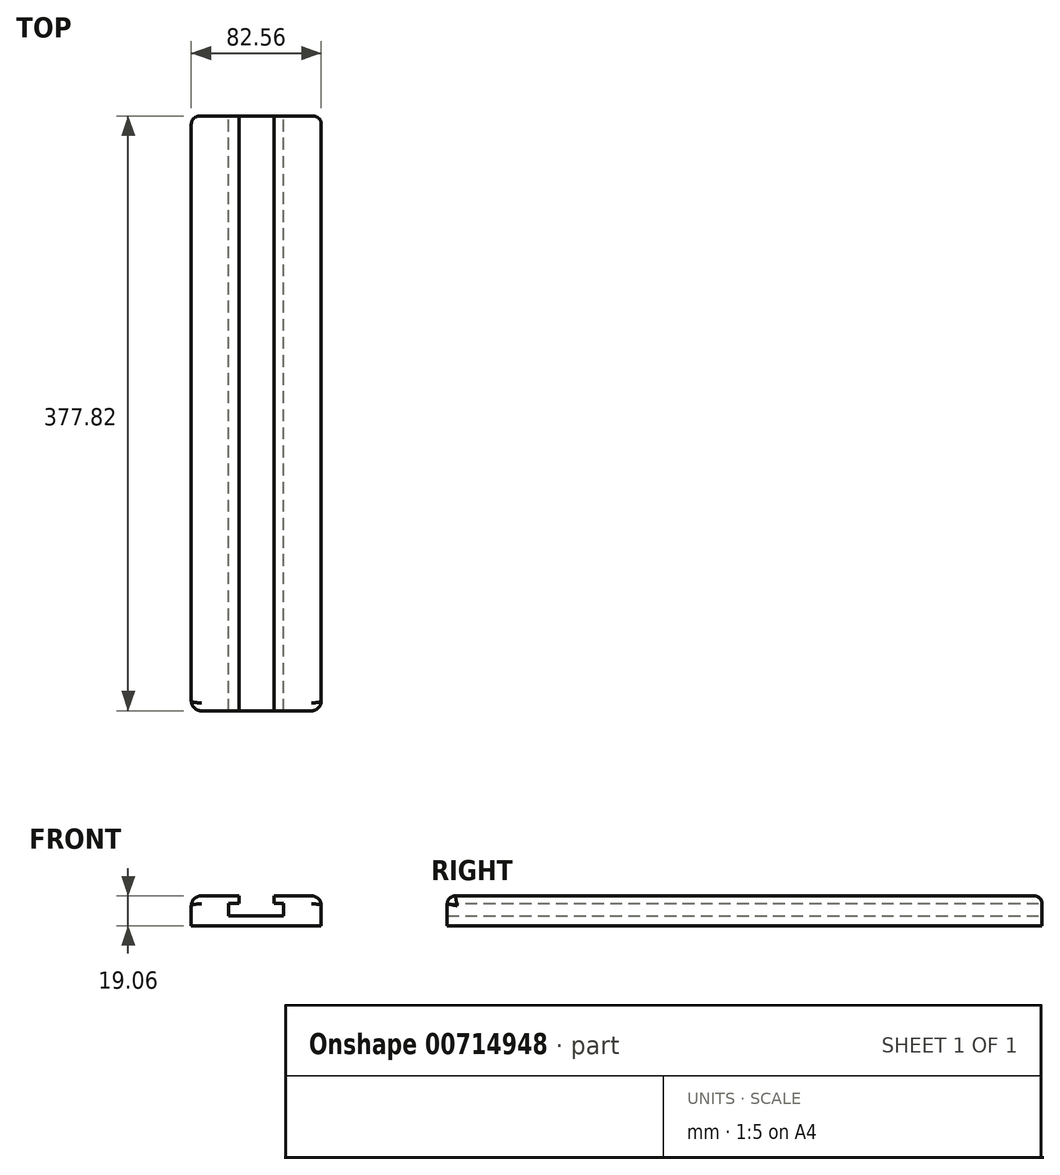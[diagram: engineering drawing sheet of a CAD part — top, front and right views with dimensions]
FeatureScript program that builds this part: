
annotation { "Feature Type Name" : "Feature", "Feature Type Description" : "" }
export const myFeature = defineFeature(function(context is Context, id is Id, definition is map)
    precondition{}
    {
        {
            var Q0;
            Q0=qCreatedBy(makeId("Front.planeOp"),FACE);
            var sketch = newSketch(context, id + "F0", { "sketchPlane" : qUnion([Q0])});
            skLineSegment(sketch, "E0.bottom", {"start": v(41.28, -9.52) * mm, "end": v(-41.28, -9.53) * mm});
            skLineSegment(sketch, "E0.left", {"start": v(41.28, -9.52) * mm, "end": v(41.28, 3.18) * mm});
            skLineSegment(sketch, "E0.right", {"start": v(-41.28, -9.53) * mm, "end": v(-41.28, 3.17) * mm});
            skPoint(sketch, "E0.middle", {"position": v(0, 0) * mm});
            skPoint(sketch, "E1.visualSharp", {"position": v(-41.28, 9.53) * mm});
            skPoint(sketch, "E2.visualSharp", {"position": v(41.28, 9.53) * mm});
            skArc(sketch, "E2.filletArc", {"start": v(41.28, 3.18) * mm, "mid": v(39.42, 7.67) * mm, "end": v(34.93, 9.53) * mm});
            skLineSegment(sketch, "E3.trimOffspring", {"start": v(-11.11, 9.53) * mm, "end": v(-34.93, 9.52) * mm});
            skLineSegment(sketch, "E4", {"start": v(34.93, 9.53) * mm, "end": v(11.11, 9.53) * mm});
            skPoint(sketch, "E5.end.orphan", {"position": v(11.11, 4.76) * mm});
            skPoint(sketch, "E6.right.end.orphan", {"position": v(10.19, 0) * mm});
            skLineSegment(sketch, "E7.bottom", {"start": v(-17.46, -3.18) * mm, "end": v(17.46, -3.17) * mm});
            skLineSegment(sketch, "E7.top", {"start": v(-17.46, 4.76) * mm, "end": v(-11.11, 4.76) * mm});
            skLineSegment(sketch, "E7.left", {"start": v(-17.46, -3.18) * mm, "end": v(-17.46, 4.76) * mm});
            skLineSegment(sketch, "E7.right", {"start": v(17.46, -3.17) * mm, "end": v(17.46, 4.76) * mm});
            skLineSegment(sketch, "E8", {"start": v(-11.11, 9.53) * mm, "end": v(-11.11, 4.76) * mm});
            skLineSegment(sketch, "E9", {"start": v(11.11, 9.53) * mm, "end": v(11.11, 4.76) * mm});
            skLineSegment(sketch, "E10.trimOffspring", {"start": v(11.11, 4.76) * mm, "end": v(17.46, 4.76) * mm});
            skPoint(sketch, "E1.filletArc.center.orphan", {"position": v(-34.93, 4.76) * mm});
            skPoint(sketch, "E11.visualSharp", {"position": v(-41.28, 9.52) * mm});
            skArc(sketch, "E11.filletArc", {"start": v(-34.93, 9.52) * mm, "mid": v(-39.42, 7.67) * mm, "end": v(-41.28, 3.17) * mm});
            skSolve(sketch);
        }
        {
            var Q0;
            Q0 = qSketchRegion(id + "F0", true);
            extrude(context, id + "F1", {"entities" : qUnion([Q0]), "endBound" : BoundingType.SYMMETRIC, "depth" : 377.82 * mm, "offsetDistance" : 25.4 * mm});
        }
        {
            var Q0;
            Q0=makeQuery(id+"F1.opExtrude","SWEPT_FACE",FACE,{"disambiguationData":[OSD([sQuery(id+"F0.wireOp",EDGE,"E0.bottom")])]});
            var sketch = newSketch(context, id + "F2", { "sketchPlane" : qUnion([Q0])});
            skLineSegment(sketch, "E12.bottom", {"start": v(-34.93, 188.91) * mm, "end": v(-34.93, 188.91) * mm});
            skLineSegment(sketch, "E12.left", {"start": v(-41.28, 182.56) * mm, "end": v(-41.28, 182.56) * mm});
            skPoint(sketch, "E13.visualSharp", {"position": v(-41.28, 188.91) * mm});
            skArc(sketch, "E13.filletArc", {"start": v(-34.93, 188.91) * mm, "mid": v(-39.42, 187.05) * mm, "end": v(-41.27, 182.56) * mm});
            skLineSegment(sketch, "E14", {"start": v(-34.93, 188.91) * mm, "end": v(-41.28, 188.91) * mm});
            skLineSegment(sketch, "E15", {"start": v(-41.28, 188.91) * mm, "end": v(-41.28, 182.56) * mm});
            skSolve(sketch);
        }
        {
            var Q0;
            Q0 = qSketchRegion(id + "F2", true);
            extrude(context, id + "F3", {"entities" : qUnion([Q0]), "operationType" : NewBodyOperationType.REMOVE, "oppositeDirection" : true, "depth" : 19.05 * mm, "offsetDistance" : 25.4 * mm});
        }
        {
            var Q0;
            Q0=makeQuery(id+"F1.opExtrude","SWEPT_FACE",FACE,{"disambiguationData":[OSD([sQuery(id+"F0.wireOp",EDGE,"E0.bottom")])]});
            var sketch = newSketch(context, id + "F4", { "sketchPlane" : qUnion([Q0])});
            skLineSegment(sketch, "E16.bottom", {"start": v(34.93, 188.91) * mm, "end": v(34.93, 188.91) * mm});
            skLineSegment(sketch, "E16.left", {"start": v(41.28, 182.56) * mm, "end": v(41.28, 182.56) * mm});
            skPoint(sketch, "E17.visualSharp", {"position": v(41.28, 188.91) * mm});
            skArc(sketch, "E17.filletArc", {"start": v(41.28, 182.56) * mm, "mid": v(39.42, 187.05) * mm, "end": v(34.93, 188.91) * mm});
            skLineSegment(sketch, "E18", {"start": v(34.93, 188.91) * mm, "end": v(41.28, 188.91) * mm});
            skLineSegment(sketch, "E19", {"start": v(41.28, 182.56) * mm, "end": v(41.28, 188.91) * mm});
            skSolve(sketch);
        }
        {
            var Q0;
            Q0 = qSketchRegion(id + "F4", true);
            extrude(context, id + "F5", {"entities" : qUnion([Q0]), "operationType" : NewBodyOperationType.REMOVE, "oppositeDirection" : true, "depth" : 19.05 * mm, "offsetDistance" : 25.4 * mm});
        }
        {
            var Q0;
            Q0=makeQuery(id+"F1.opExtrude","CAP_EDGE",EDGE,{"disambiguationData":[OSD([sQuery(id+"F0.wireOp",EDGE,"E3.trimOffspring")])],"isStart":false});
            var Q1;
            Q1=makeQuery(id+"F1.opExtrude","CAP_EDGE",EDGE,{"disambiguationData":[OSD([sQuery(id+"F0.wireOp",EDGE,"E4")])],"isStart":false});
            var Q2;
            Q2=makeQuery(id+"F1.opExtrude","CAP_EDGE",EDGE,{"disambiguationData":[OSD([sQuery(id+"F0.wireOp",EDGE,"E0.left")])],"isStart":true});
            var Q3;
            Q3=makeQuery(id+"F1.opExtrude","CAP_EDGE",EDGE,{"disambiguationData":[OSD([sQuery(id+"F0.wireOp",EDGE,"E0.right")])],"isStart":true});
            fillet(context, id + "F6", {"entities" : qUnion([Q0, Q1, Q2, Q3]), "radius" : 5.08 * mm, "tangentPropagation" : true, "allowEdgeOverflow" : false});
        }
    });
